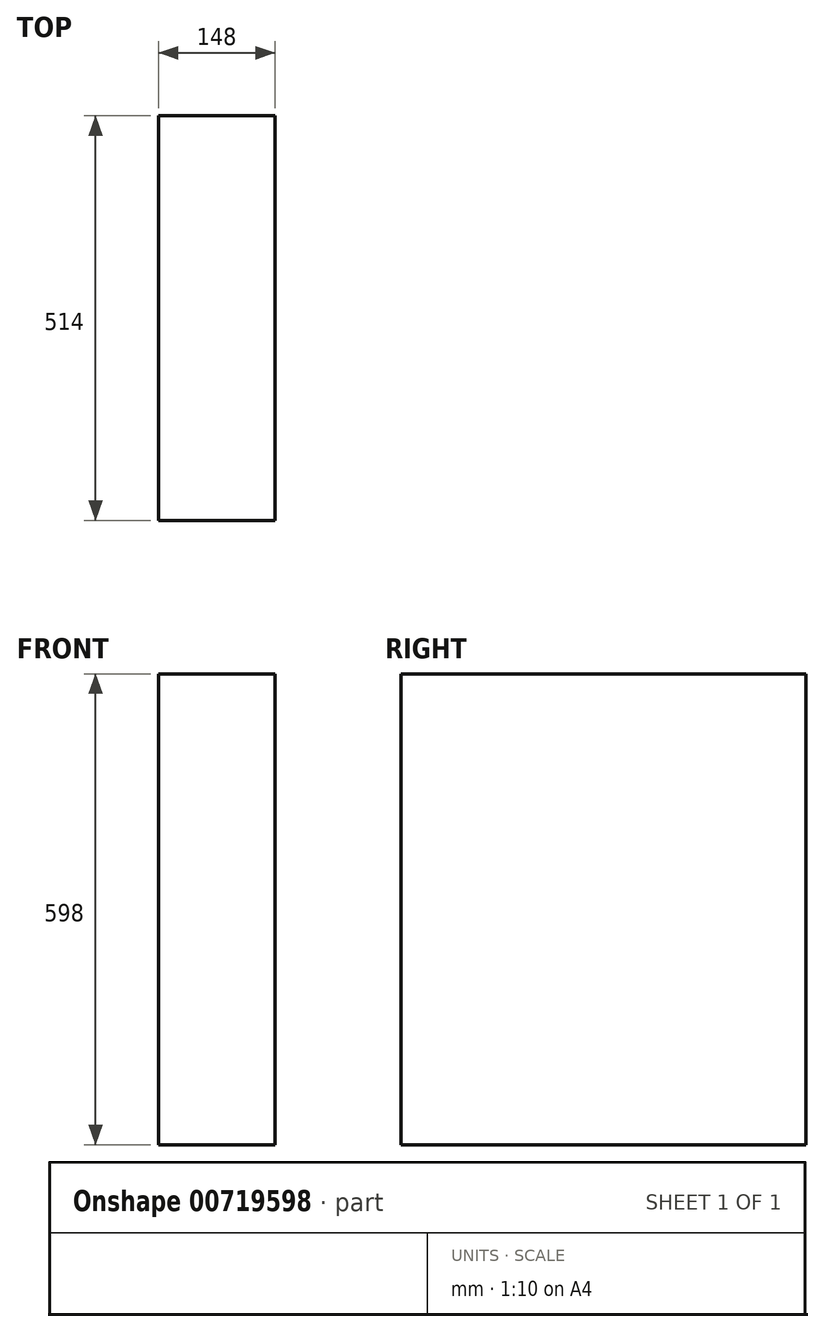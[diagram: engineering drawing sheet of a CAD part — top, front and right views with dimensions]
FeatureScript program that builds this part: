
annotation { "Feature Type Name" : "Feature", "Feature Type Description" : "" }
export const myFeature = defineFeature(function(context is Context, id is Id, definition is map)
    precondition{}
    {
        {
            var Q0;
            Q0=qCreatedBy(makeId("Front.planeOp"),FACE);
            var sketch = newSketch(context, id + "F0", { "sketchPlane" : qUnion([Q0])});
            skLineSegment(sketch, "E0.bottom", {"start": v(0, 0) * mm, "end": v(148, 0) * mm});
            skLineSegment(sketch, "E0.top", {"start": v(0, 598) * mm, "end": v(148, 598) * mm});
            skLineSegment(sketch, "E0.left", {"start": v(0, 0) * mm, "end": v(0, 598) * mm});
            skLineSegment(sketch, "E0.right", {"start": v(148, 0) * mm, "end": v(148, 598) * mm});
            skSolve(sketch);
        }
        {
            var Q0;
            Q0=makeQuery(id+"F0.imprint","IMPRINT",FACE,{"disambiguationData":[TD([[makeQuery(id+"F0.imprint","IMPRINT",EDGE,{"derivedFrom":sQuery(id+"F0.wireOp",EDGE,"E0.bottom")}),1.0]])]});
            extrude(context, id + "F1", {"entities" : qUnion([Q0]), "oppositeDirection" : true, "depth" : 514 * mm, "offsetDistance" : 25 * mm});
        }
    });
